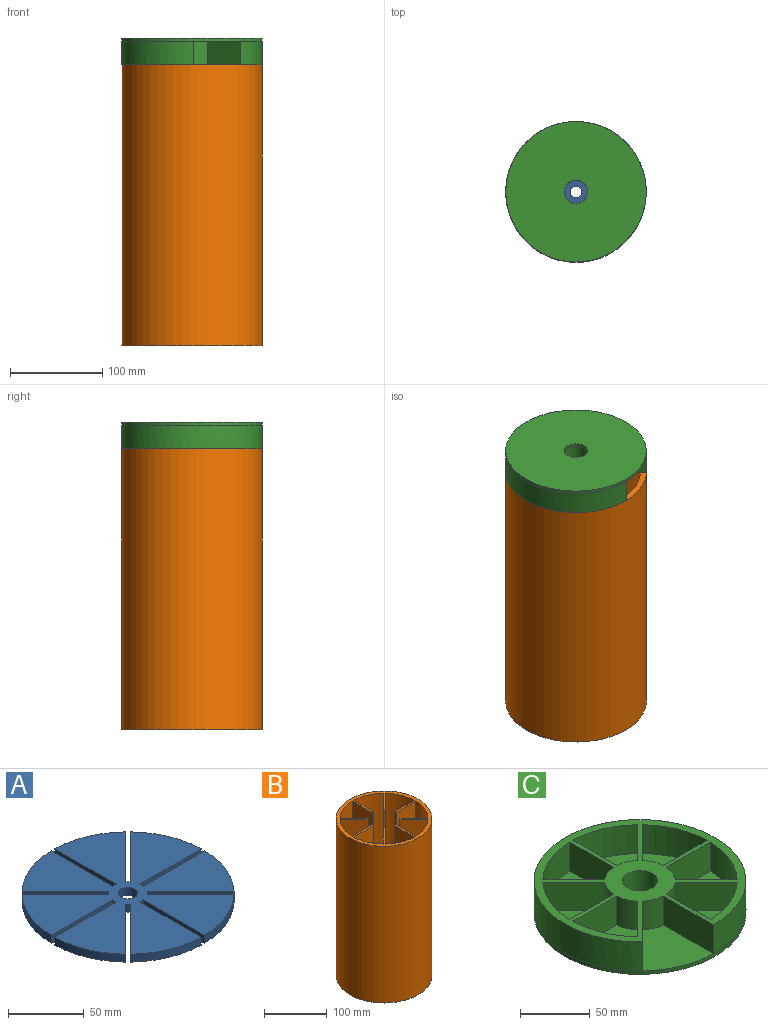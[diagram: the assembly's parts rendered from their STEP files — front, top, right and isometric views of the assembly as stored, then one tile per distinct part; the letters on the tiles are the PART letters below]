
ASSEMBLY  parts=3 mates=2
PART A: 35 faces, bbox 139.7x139.7x6.4 mm
  f0: plane 57.23x6.35mm, normal (1,0,0), area 363.4mm2, adj f1,f32,f33,f34
  f1: cylinder r=69.85mm len=46.67mm, axis (0,0,-1), area 328.2mm2, adj f0,f2,f33,f34
  f2: plane 40.47x40.47mm, normal (-0.71,-0.71,0), area 363.4mm2, adj f1,f3,f33,f34
  f3: cylinder r=12.7mm len=6.35mm, axis (0,0,-1), area 20.2mm2, adj f2,f4,f33,f34
  f4: plane 40.47x40.47mm, normal (0.71,0.71,0), area 363.4mm2, adj f3,f5,f33,f34
  f5: cylinder r=69.85mm len=46.67mm, axis (0,0,-1), area 328.2mm2, adj f4,f6,f33,f34
  f6: plane 57.23x6.35mm, normal (0,-1,0), area 363.4mm2, adj f5,f7,f33,f34
  f7: cylinder r=12.7mm len=6.35mm, axis (0,0,-1), area 20.2mm2, adj f6,f8,f33,f34
  f8: plane 57.23x6.35mm, normal (0,1,0), area 363.4mm2, adj f7,f9,f33,f34
  f9: cylinder r=69.85mm len=46.67mm, axis (0,0,-1), area 328.2mm2, adj f8,f10,f33,f34
  f10: plane 40.47x40.47mm, normal (0.71,-0.71,0), area 363.4mm2, adj f9,f11,f33,f34
  f11: cylinder r=12.7mm len=6.35mm, axis (0,0,-1), area 20.2mm2, adj f10,f12,f33,f34
  f12: plane 40.47x40.47mm, normal (-0.71,0.71,0), area 363.4mm2, adj f11,f13,f33,f34
  f13: cylinder r=69.85mm len=46.67mm, axis (0,0,-1), area 328.2mm2, adj f12,f14,f33,f34
  f14: plane 57.23x6.35mm, normal (1,0,0), area 363.4mm2, adj f13,f15,f33,f34
  f15: cylinder r=12.7mm len=6.35mm, axis (0,0,-1), area 20.2mm2, adj f14,f16,f33,f34
  f16: plane 57.23x6.35mm, normal (-1,0,0), area 363.4mm2, adj f15,f17,f33,f34
  f17: cylinder r=69.85mm len=46.67mm, axis (0,0,-1), area 328.2mm2, adj f16,f18,f33,f34
  f18: plane 40.47x40.47mm, normal (0.71,0.71,0), area 363.4mm2, adj f17,f19,f33,f34
  f19: cylinder r=12.7mm len=6.35mm, axis (0,0,-1), area 20.2mm2, adj f18,f20,f33,f34
  f20: plane 40.47x40.47mm, normal (-0.71,-0.71,0), area 363.4mm2, adj f19,f21,f33,f34
  f21: cylinder r=69.85mm len=46.67mm, axis (0,0,-1), area 328.2mm2, adj f20,f22,f33,f34
  f22: plane 57.23x6.35mm, normal (0,1,0), area 363.4mm2, adj f21,f23,f33,f34
  f23: cylinder r=12.7mm len=6.35mm, axis (0,0,-1), area 20.2mm2, adj f22,f24,f33,f34
  f24: plane 57.23x6.35mm, normal (0,-1,0), area 363.4mm2, adj f23,f25,f33,f34
  f25: cylinder r=69.85mm len=46.67mm, axis (0,0,-1), area 328.2mm2, adj f24,f26,f33,f34
  f26: plane 40.47x40.47mm, normal (-0.71,0.71,0), area 363.4mm2, adj f25,f27,f33,f34
  f27: cylinder r=12.7mm len=6.35mm, axis (0,0,-1), area 20.2mm2, adj f26,f28,f33,f34
  f28: plane 40.47x40.47mm, normal (0.71,-0.71,0), area 363.4mm2, adj f27,f29,f33,f34
  f29: cylinder r=69.85mm len=46.67mm, axis (0,0,-1), area 328.2mm2, adj f28,f30,f33,f34
  f30: plane 57.23x6.35mm, normal (-1,0,0), area 363.4mm2, adj f29,f32,f33,f34
  f31: cylinder r=6.35mm len=12.7mm, axis (0,0,-1), area 253.4mm2, adj f33,f34
  f32: cylinder r=12.7mm len=6.35mm, axis (0,0,-1), area 20.2mm2, adj f0,f30,f33,f34
  f33: plane 139.66x139.66mm, normal (0,0,1), area 13748.9mm2, adj f0,f1,f2,f3,f4,f5,f6,f7
  f34: plane 139.66x139.66mm, normal (0,0,-1), area 13748.9mm2, adj f0,f1,f2,f3,f4,f5,f6,f7
PART B: 35 faces, bbox 152.4x152.4x304.8 mm
  f0: plane 304.8x2.25mm, normal (-0.71,-0.71,0), area 967.7mm2, adj f1,f32,f33,f34
  f1: plane 304.8x31.43mm, normal (0.71,-0.71,0), area 13548.4mm2, adj f0,f2,f33,f34
  f2: cylinder r=69.85mm len=304.8mm, axis (0,0,-1), area 15753.5mm2, adj f1,f3,f33,f34
  f3: plane 304.8x44.45mm, normal (0,1,0), area 13548.4mm2, adj f2,f4,f33,f34
  f4: plane 304.8x3.18mm, normal (-1,0,0), area 967.7mm2, adj f3,f5,f33,f34
  f5: plane 304.8x44.45mm, normal (0,-1,0), area 13548.4mm2, adj f4,f6,f33,f34
  f6: cylinder r=69.85mm len=304.8mm, axis (0,0,-1), area 15753.5mm2, adj f5,f7,f33,f34
  f7: plane 304.8x31.43mm, normal (0.71,0.71,0), area 13548.4mm2, adj f6,f8,f33,f34
  f8: plane 304.8x2.25mm, normal (-0.71,0.71,0), area 967.7mm2, adj f7,f9,f33,f34
  f9: plane 304.8x31.43mm, normal (-0.71,-0.71,0), area 13548.4mm2, adj f8,f10,f33,f34
  f10: cylinder r=69.85mm len=304.8mm, axis (0,0,-1), area 15753.5mm2, adj f9,f11,f33,f34
  f11: plane 304.8x44.45mm, normal (1,0,0), area 13548.4mm2, adj f10,f12,f33,f34
  f12: plane 304.8x3.18mm, normal (0,1,0), area 967.7mm2, adj f11,f13,f33,f34
  f13: plane 304.8x44.45mm, normal (-1,0,0), area 13548.4mm2, adj f12,f14,f33,f34
  f14: cylinder r=69.85mm len=304.8mm, axis (0,0,-1), area 15753.5mm2, adj f13,f15,f33,f34
  f15: plane 304.8x31.43mm, normal (0.71,-0.71,0), area 13548.4mm2, adj f14,f16,f33,f34
  f16: plane 304.8x2.25mm, normal (0.71,0.71,0), area 967.7mm2, adj f15,f17,f33,f34
  f17: plane 304.8x31.43mm, normal (-0.71,0.71,0), area 13548.4mm2, adj f16,f18,f33,f34
  f18: cylinder r=69.85mm len=304.8mm, axis (0,0,-1), area 15753.5mm2, adj f17,f19,f33,f34
  f19: plane 304.8x44.45mm, normal (0,-1,0), area 13548.4mm2, adj f18,f20,f33,f34
  f20: plane 304.8x3.18mm, normal (1,0,0), area 967.7mm2, adj f19,f21,f33,f34
  f21: plane 304.8x44.45mm, normal (0,1,0), area 13548.4mm2, adj f20,f22,f33,f34
  f22: cylinder r=69.85mm len=304.8mm, axis (0,0,-1), area 15753.5mm2, adj f21,f23,f33,f34
  f23: plane 304.8x31.43mm, normal (-0.71,-0.71,0), area 13548.4mm2, adj f22,f24,f33,f34
  f24: plane 304.8x2.25mm, normal (0.71,-0.71,0), area 967.7mm2, adj f23,f25,f33,f34
  f25: plane 304.8x31.43mm, normal (0.71,0.71,0), area 13548.4mm2, adj f24,f26,f33,f34
  f26: cylinder r=69.85mm len=304.8mm, axis (0,0,-1), area 15753.5mm2, adj f25,f27,f33,f34
  f27: plane 304.8x44.45mm, normal (-1,0,0), area 13548.4mm2, adj f26,f28,f33,f34
  f28: plane 304.8x3.18mm, normal (0,-1,0), area 967.7mm2, adj f27,f29,f33,f34
  f29: plane 304.8x44.45mm, normal (1,0,0), area 13548.4mm2, adj f28,f30,f33,f34
  f30: cylinder r=69.85mm len=304.8mm, axis (0,0,-1), area 15753.5mm2, adj f29,f32,f33,f34
  f31: cylinder r=76.2mm len=304.8mm, axis (0,0,-1), area 145931.8mm2, adj f33,f34
  f32: plane 304.8x31.43mm, normal (-0.71,0.71,0), area 13548.4mm2, adj f0,f30,f33,f34
  f33: plane 152.4x152.4mm, normal (0,0,1), area 4042.9mm2, adj f0,f1,f2,f3,f4,f5,f6,f7
  f34: plane 152.4x152.4mm, normal (0,0,-1), area 4042.9mm2, adj f0,f1,f2,f3,f4,f5,f6,f7
PART C: 48 faces, bbox 152.4x152.4x28.6 mm
  f0: plane 25.38x13.51mm, normal (0,0,-1), area 0.8mm2, adj f32,f39
  f1: cylinder r=69.85mm len=46.67mm, axis (0,0,-1), area 1312.8mm2, adj f2,f33,f34,f36
  f2: plane 44.48x25.4mm, normal (-1,0,0), area 1129.8mm2, adj f1,f3,f34,f36
  f3: cylinder r=25.4mm len=25.4mm, axis (0,0,-1), area 426mm2, adj f2,f33,f34,f36
  f4: plane 31.45x31.45mm, normal (-0.71,-0.71,0), area 1129.8mm2, adj f5,f25,f34,f47
  f5: cylinder r=25.4mm len=25.4mm, axis (0,0,-1), area 426mm2, adj f4,f6,f34,f47
  f6: plane 44.48x25.4mm, normal (0,1,0), area 1129.8mm2, adj f5,f25,f34,f47
  f7: plane 31.45x31.45mm, normal (-0.71,0.71,0), area 1129.8mm2, adj f8,f26,f34,f46
  f8: cylinder r=25.4mm len=25.4mm, axis (0,0,-1), area 426mm2, adj f7,f9,f34,f46
  f9: plane 44.48x25.4mm, normal (1,0,0), area 1129.8mm2, adj f8,f26,f34,f46
  f10: plane 44.48x25.4mm, normal (0,1,0), area 1129.8mm2, adj f11,f27,f34,f45
  f11: cylinder r=25.4mm len=25.4mm, axis (0,0,-1), area 426mm2, adj f10,f12,f34,f45
  f12: plane 31.45x31.45mm, normal (0.71,-0.71,0), area 1129.8mm2, adj f11,f27,f34,f45
  f13: plane 31.45x31.45mm, normal (0.71,0.71,0), area 1129.8mm2, adj f14,f28,f34,f44
  f14: cylinder r=25.4mm len=25.4mm, axis (0,0,-1), area 426mm2, adj f13,f15,f34,f44
  f15: plane 44.48x25.4mm, normal (0,-1,0), area 1129.8mm2, adj f14,f28,f34,f44
  f16: plane 44.48x25.4mm, normal (1,0,0), area 1129.8mm2, adj f17,f29,f34,f43
  f17: cylinder r=25.4mm len=25.4mm, axis (0,0,-1), area 426mm2, adj f16,f18,f34,f43
  f18: plane 31.45x31.45mm, normal (-0.71,-0.71,0), area 1129.8mm2, adj f17,f29,f34,f43
  f19: plane 44.48x25.4mm, normal (0,-1,0), area 1129.8mm2, adj f20,f30,f34,f42
  f20: cylinder r=25.4mm len=25.4mm, axis (0,0,-1), area 426mm2, adj f19,f21,f34,f42
  f21: plane 31.45x31.45mm, normal (-0.71,0.71,0), area 1129.8mm2, adj f20,f30,f34,f42
  f22: plane 35.93x35.93mm, normal (0.71,-0.71,0), area 1290.6mm2, adj f23,f31,f34,f41
  f23: cylinder r=25.4mm len=25.4mm, axis (0,0,-1), area 426mm2, adj f22,f24,f34,f41
  f24: plane 50.8x25.4mm, normal (-1,0,0), area 1290.4mm2, adj f23,f31,f34,f41
  f25: cylinder r=69.85mm len=46.67mm, axis (0,0,-1), area 1312.8mm2, adj f4,f6,f34,f47
  f26: cylinder r=69.85mm len=46.67mm, axis (0,0,-1), area 1312.8mm2, adj f7,f9,f34,f46
  f27: cylinder r=69.85mm len=46.67mm, axis (0,0,-1), area 1312.8mm2, adj f10,f12,f34,f45
  f28: cylinder r=69.85mm len=46.67mm, axis (0,0,-1), area 1312.8mm2, adj f13,f15,f34,f44
  f29: cylinder r=69.85mm len=46.67mm, axis (0,0,-1), area 1312.8mm2, adj f16,f18,f34,f43
  f30: cylinder r=69.85mm len=46.67mm, axis (0,0,-1), area 1312.8mm2, adj f19,f21,f34,f42
  f31: cylinder r=76.2mm len=152.4mm, axis (0,0,-1), area 10722.1mm2, adj f22,f24,f34,f35,f41
  f32: cylinder r=12.7mm len=25.4mm, axis (0,0,-1), area 2026.8mm2, adj f0,f34,f40
  f33: plane 31.45x31.45mm, normal (0.71,0.71,0), area 1129.8mm2, adj f1,f3,f34,f36
  f34: plane 152.4x152.4mm, normal (0,0,1), area 5220.5mm2, adj f1,f2,f3,f4,f5,f6,f7,f8
  f35: plane 152.25x80.97mm, normal (0,0,-1), area 4.8mm2, adj f31,f38
  f36: plane 50.78x46.67mm, normal (0,0,1), area 1521.5mm2, adj f1,f2,f3,f33
  f37: plane 152.4x152.4mm, normal (0,0,-1), area 17734.8mm2, adj f38,f39
  f38: cylinder r=76.2mm len=152.4mm, axis (0,0,1), area 1520.1mm2, adj f35,f37,f41
  f39: cylinder r=12.7mm len=25.4mm, axis (0,0,1), area 253.4mm2, adj f0,f37,f40
  f40: plane 25.38x13.51mm, normal (0,0,1), area 0.8mm2, adj f32,f39
  f41: plane 152.25x80.97mm, normal (0,0,1), area 1868.7mm2, adj f22,f23,f24,f31,f38
  f42: plane 50.78x46.67mm, normal (0,0,1), area 1521.5mm2, adj f19,f20,f21,f30
  f43: plane 50.78x46.67mm, normal (0,0,1), area 1521.5mm2, adj f16,f17,f18,f29
  f44: plane 50.78x46.67mm, normal (0,0,1), area 1521.5mm2, adj f13,f14,f15,f28
  f45: plane 50.78x46.67mm, normal (0,0,1), area 1521.5mm2, adj f10,f11,f12,f27
  f46: plane 50.78x46.67mm, normal (0,0,1), area 1521.5mm2, adj f7,f8,f9,f26
  f47: plane 50.78x46.67mm, normal (0,0,1), area 1521.5mm2, adj f4,f5,f6,f25
PLACE A t=(-6.87,-49.57,-16.25)mm
PLACE B t=(-6.87,-49.57,-6.65)mm
PLACE C rot(axis=(0,1,0),180deg) t=(-6.88,-49.61,171.15)mm
MATE cylindrical C.f31 <-> B.f31  axis (0,0,-1) through (-6.87,-49.57,145.75)mm
MATE cylindrical A.f17 <-> B.f14  axis (0,0,1) through (-6.87,-49.57,-9.9)mm
